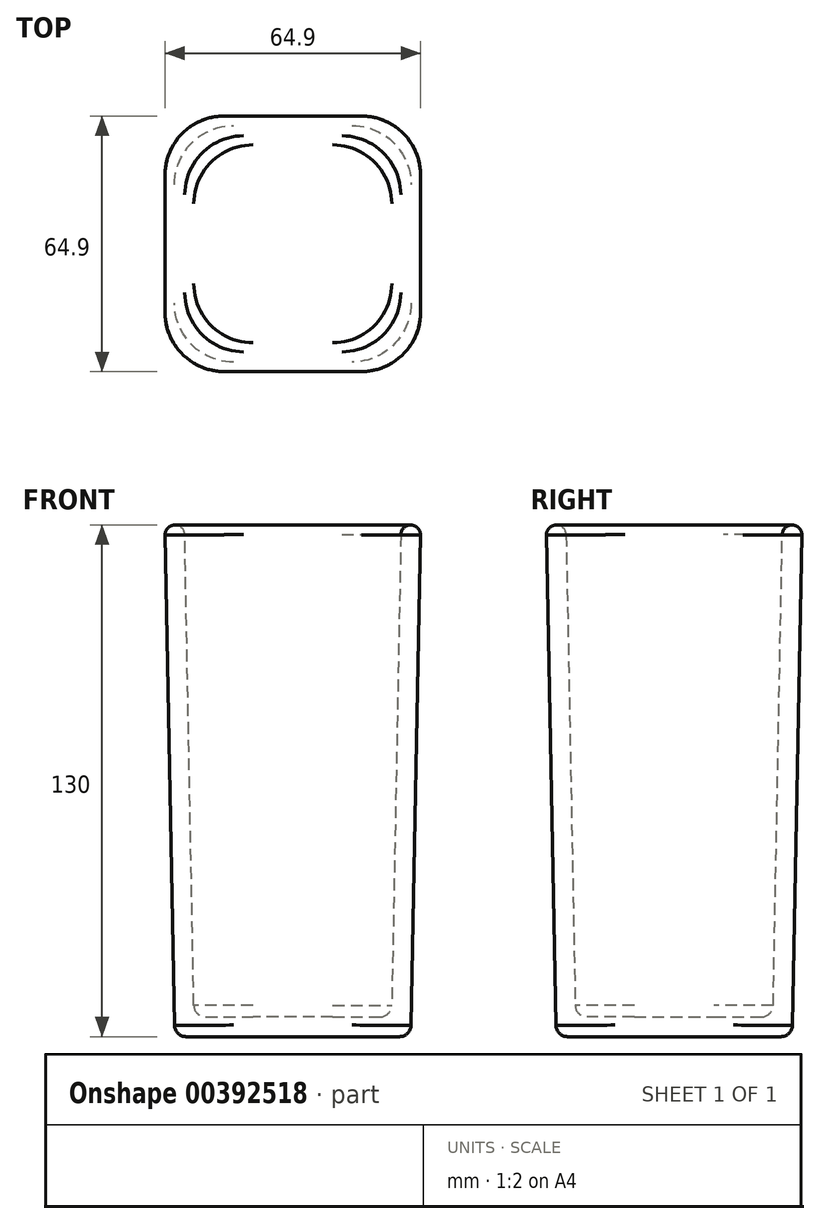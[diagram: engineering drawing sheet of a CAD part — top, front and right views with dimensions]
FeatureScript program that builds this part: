
annotation { "Feature Type Name" : "Feature", "Feature Type Description" : "" }
export const myFeature = defineFeature(function(context is Context, id is Id, definition is map)
    precondition{}
    {
        {
            var Q0;
            Q0=qCreatedBy(makeId("Top.planeOp"),FACE);
            var sketch = newSketch(context, id + "F0", { "sketchPlane" : qUnion([Q0])});
            skLineSegment(sketch, "E0.bottom", {"start": v(30, -30) * mm, "end": v(-30, -30) * mm});
            skLineSegment(sketch, "E0.top", {"start": v(30, 30) * mm, "end": v(-30, 30) * mm});
            skLineSegment(sketch, "E0.left", {"start": v(30, -30) * mm, "end": v(30, 30) * mm});
            skLineSegment(sketch, "E0.right", {"start": v(-30, -30) * mm, "end": v(-30, 30) * mm});
            skPoint(sketch, "E0.middle", {"position": v(0, 0) * mm});
            skSolve(sketch);
        }
        {
            var Q0;
            Q0=qCreatedBy(makeId("Top.planeOp"),FACE);
            cPlane(context, id + "F1", {"entities" : qUnion([Q0]), "cplaneType" : CPlaneType.OFFSET, "offset" : 130 * mm, "width" : 150 * mm, "height" : 150 * mm});
        }
        {
            var Q0;
            Q0=qCreatedBy(id+"F1.planeOp",FACE);
            var sketch = newSketch(context, id + "F2", { "sketchPlane" : qUnion([Q0])});
            skLineSegment(sketch, "E1.bottom", {"start": v(32.5, -32.5) * mm, "end": v(-32.5, -32.5) * mm});
            skLineSegment(sketch, "E1.top", {"start": v(32.5, 32.5) * mm, "end": v(-32.5, 32.5) * mm});
            skLineSegment(sketch, "E1.left", {"start": v(32.5, -32.5) * mm, "end": v(32.5, 32.5) * mm});
            skLineSegment(sketch, "E1.right", {"start": v(-32.5, -32.5) * mm, "end": v(-32.5, 32.5) * mm});
            skPoint(sketch, "E1.middle", {"position": v(0, 0) * mm});
            skSolve(sketch);
        }
        {
            var Q0;
            Q0=makeQuery(id+"F0.imprint","IMPRINT",FACE,{"disambiguationData":[TD([[makeQuery(id+"F0.imprint","IMPRINT",EDGE,{"derivedFrom":sQuery(id+"F0.wireOp",EDGE,"E0.bottom")}),-1.0]])]});
            var Q1;
            Q1=makeQuery(id+"F2.imprint","IMPRINT",FACE,{"disambiguationData":[TD([[makeQuery(id+"F2.imprint","IMPRINT",EDGE,{"derivedFrom":sQuery(id+"F2.wireOp",EDGE,"E1.bottom")}),-1.0]])]});
            loft(context, id + "F3", {"sheetProfilesArray" : [{ "sheetProfileEntities" : qUnion([Q0]) }, { "sheetProfileEntities" : qUnion([Q1]) }]});
        }
        {
            var Q0;
            Q0=makeQuery(id+"F3.opLoft","CAP_FACE",FACE,{"disambiguationData":[OSD([makeQuery(id+"F2.imprint","IMPRINT",FACE,{"disambiguationData":[TD([[makeQuery(id+"F2.imprint","IMPRINT",EDGE,{"derivedFrom":sQuery(id+"F2.wireOp",EDGE,"E1.bottom")}),-1.0]])]})])],"isStart":true});
            shell(context, id + "F4", {"entities" : qUnion([Q0]), "thickness" : 5 * mm});
        }
        {
            var Q0;
            Q0=makeQuery(id+"F3.opLoft","SWEPT_EDGE",EDGE,{"disambiguationData":[OSD([sQuery(id+"F0.wireOp",EDGE,"E0.bottom"),sQuery(id+"F0.wireOp",EDGE,"E0.left"),sQuery(id+"F2.wireOp",EDGE,"E1.bottom"),sQuery(id+"F2.wireOp",EDGE,"E1.left")])]});
            var Q1;
            Q1=makeQuery(id+"F3.opLoft","SWEPT_EDGE",EDGE,{"disambiguationData":[OSD([sQuery(id+"F0.wireOp",EDGE,"E0.top"),sQuery(id+"F0.wireOp",EDGE,"E0.left"),sQuery(id+"F2.wireOp",EDGE,"E1.top"),sQuery(id+"F2.wireOp",EDGE,"E1.left")])]});
            var Q2;
            Q2=makeQuery(id+"F3.opLoft","SWEPT_EDGE",EDGE,{"disambiguationData":[OSD([sQuery(id+"F0.wireOp",EDGE,"E0.top"),sQuery(id+"F0.wireOp",EDGE,"E0.right"),sQuery(id+"F2.wireOp",EDGE,"E1.top"),sQuery(id+"F2.wireOp",EDGE,"E1.right")])]});
            var Q3;
            Q3=makeQuery(id+"F3.opLoft","SWEPT_EDGE",EDGE,{"disambiguationData":[OSD([sQuery(id+"F0.wireOp",EDGE,"E0.bottom"),sQuery(id+"F0.wireOp",EDGE,"E0.right"),sQuery(id+"F2.wireOp",EDGE,"E1.bottom"),sQuery(id+"F2.wireOp",EDGE,"E1.right")])]});
            var Q4;
            Q4=makeQuery(id+"F4.opShell","OFFSET_EDGE",EDGE,{"disambiguationData":[OSD([sQuery(id+"F0.wireOp",EDGE,"E0.top"),sQuery(id+"F0.wireOp",EDGE,"E0.right"),sQuery(id+"F2.wireOp",EDGE,"E1.top"),sQuery(id+"F2.wireOp",EDGE,"E1.right")])]});
            var Q5;
            Q5=makeQuery(id+"F4.opShell","OFFSET_EDGE",EDGE,{"disambiguationData":[OSD([sQuery(id+"F0.wireOp",EDGE,"E0.bottom"),sQuery(id+"F0.wireOp",EDGE,"E0.right"),sQuery(id+"F2.wireOp",EDGE,"E1.bottom"),sQuery(id+"F2.wireOp",EDGE,"E1.right")])]});
            var Q6;
            Q6=makeQuery(id+"F4.opShell","OFFSET_EDGE",EDGE,{"disambiguationData":[OSD([sQuery(id+"F0.wireOp",EDGE,"E0.bottom"),sQuery(id+"F0.wireOp",EDGE,"E0.left"),sQuery(id+"F2.wireOp",EDGE,"E1.bottom"),sQuery(id+"F2.wireOp",EDGE,"E1.left")])]});
            var Q7;
            Q7=makeQuery(id+"F4.opShell","OFFSET_EDGE",EDGE,{"disambiguationData":[OSD([sQuery(id+"F0.wireOp",EDGE,"E0.top"),sQuery(id+"F0.wireOp",EDGE,"E0.left"),sQuery(id+"F2.wireOp",EDGE,"E1.top"),sQuery(id+"F2.wireOp",EDGE,"E1.left")])]});
            fillet(context, id + "F5", {"entities" : qUnion([Q0, Q1, Q2, Q3, Q4, Q5, Q6, Q7]), "radius" : 15 * mm, "tangentPropagation" : true, "allowEdgeOverflow" : false});
        }
        {
            var Q0;
            Q0=makeQuery(id+"F3.opLoft","MID_CAP_EDGE",EDGE,{"disambiguationData":[OSD([sQuery(id+"F0.wireOp",EDGE,"E0.bottom"),sQuery(id+"F0.wireOp",EDGE,"E0.left"),sQuery(id+"F0.wireOp",EDGE,"E0.right")])],"capPos":0.0});
            var Q1;
            Q1=makeQuery(id+"F3.opLoft","MID_CAP_EDGE",EDGE,{"disambiguationData":[OSD([sQuery(id+"F0.wireOp",EDGE,"E0.bottom"),sQuery(id+"F0.wireOp",EDGE,"E0.top"),sQuery(id+"F0.wireOp",EDGE,"E0.right")])],"capPos":0.0});
            var Q2;
            Q2=makeQuery(id+"F3.opLoft","MID_CAP_EDGE",EDGE,{"disambiguationData":[OSD([sQuery(id+"F0.wireOp",EDGE,"E0.top"),sQuery(id+"F0.wireOp",EDGE,"E0.left"),sQuery(id+"F0.wireOp",EDGE,"E0.right")])],"capPos":0.0});
            var Q3;
            Q3=makeQuery(id+"F3.opLoft","MID_CAP_EDGE",EDGE,{"disambiguationData":[OSD([sQuery(id+"F0.wireOp",EDGE,"E0.bottom"),sQuery(id+"F0.wireOp",EDGE,"E0.top"),sQuery(id+"F0.wireOp",EDGE,"E0.left")])],"capPos":0.0});
            var Q4;
            Q4=makeQuery(id+"F4.opShell","OFFSET_EDGE",EDGE,{"disambiguationData":[OSD([sQuery(id+"F0.wireOp",EDGE,"E0.bottom"),sQuery(id+"F0.wireOp",EDGE,"E0.left"),sQuery(id+"F0.wireOp",EDGE,"E0.right")])]});
            fillet(context, id + "F6", {"entities" : qUnion([Q0, Q1, Q2, Q3, Q4]), "radius" : 3 * mm, "tangentPropagation" : true, "allowEdgeOverflow" : false});
        }
        {
            var Q0;
            Q0=makeQuery(id+"F3.opLoft","MID_CAP_EDGE",EDGE,{"disambiguationData":[OSD([sQuery(id+"F2.wireOp",EDGE,"E1.bottom"),sQuery(id+"F2.wireOp",EDGE,"E1.top"),sQuery(id+"F2.wireOp",EDGE,"E1.left")])],"capPos":1.0});
            var Q1;
            Q1=makeQuery(id+"F4.opShell","OFFSET_EDGE",EDGE,{"disambiguationData":[OSD([sQuery(id+"F2.wireOp",EDGE,"E1.bottom"),sQuery(id+"F2.wireOp",EDGE,"E1.top"),sQuery(id+"F2.wireOp",EDGE,"E1.left")])]});
            fillet(context, id + "F7", {"entities" : qUnion([Q0, Q1]), "radius" : 2.5 * mm, "tangentPropagation" : true, "allowEdgeOverflow" : false});
        }
    });
